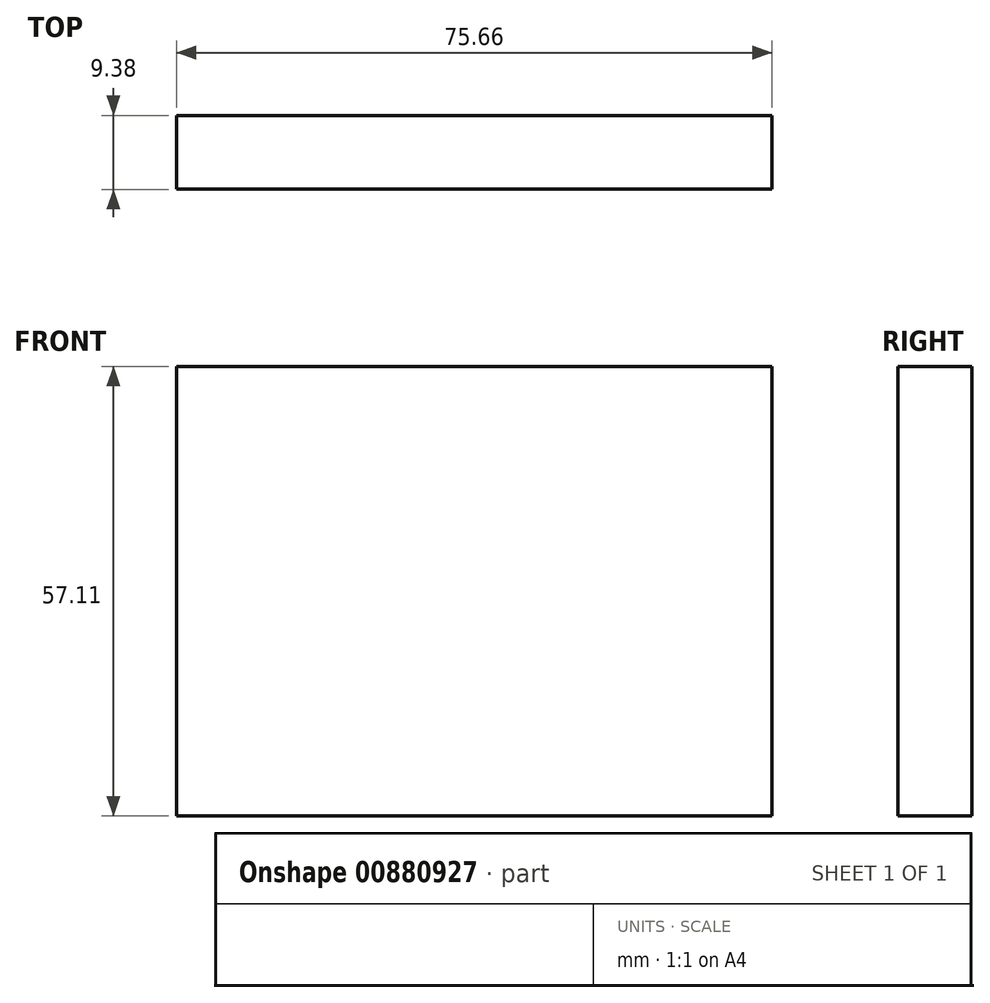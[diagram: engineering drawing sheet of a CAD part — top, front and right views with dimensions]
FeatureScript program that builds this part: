
annotation { "Feature Type Name" : "Feature", "Feature Type Description" : "" }
export const myFeature = defineFeature(function(context is Context, id is Id, definition is map)
    precondition{}
    {
        {
            var Q0;
            Q0=qCreatedBy(makeId("Top.planeOp"),FACE);
            var sketch = newSketch(context, id + "F0", { "sketchPlane" : qUnion([Q0])});
            skLineSegment(sketch, "E0.bottom", {"start": v(-24.53, 48.82) * mm, "end": v(51.13, 48.82) * mm});
            skLineSegment(sketch, "E0.top", {"start": v(-24.53, 39.44) * mm, "end": v(51.13, 39.44) * mm});
            skLineSegment(sketch, "E0.left", {"start": v(-24.53, 48.82) * mm, "end": v(-24.53, 39.44) * mm});
            skLineSegment(sketch, "E0.right", {"start": v(51.13, 48.82) * mm, "end": v(51.13, 39.44) * mm});
            skSolve(sketch);
        }
        {
            var Q0;
            Q0 = qSketchRegion(id + "F0", true);
            var sketch = newSketch(context, id + "F1", { "sketchPlane" : qUnion([Q0])});
            skSolve(sketch);
        }
        {
            var Q0;
            Q0=makeQuery(id+"F1.imprint","IMPRINT",FACE,{"disambiguationData":[TD([[makeQuery(id+"F1.imprint","IMPRINT",EDGE,{"derivedFrom":makeQuery(id+"F0.imprint","IMPRINT",EDGE,{"derivedFrom":sQuery(id+"F0.wireOp",EDGE,"E0.bottom")})}),-1.0]])]});
            extrude(context, id + "F2", {"entities" : qUnion([Q0]), "depth" : 57.1 * mm, "offsetDistance" : 25 * mm});
        }
    });
